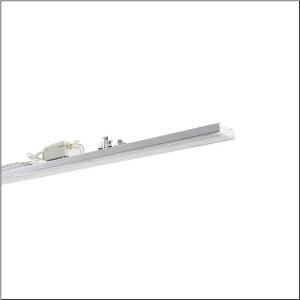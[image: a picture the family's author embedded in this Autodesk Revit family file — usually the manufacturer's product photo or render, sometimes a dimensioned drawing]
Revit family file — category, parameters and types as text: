
# Revit family: licross_r__21_recessed_mo_52te1edn495g_06d0
name_source: partatom
category: Lighting Fixtures
units: mm (PartAtom-declared; Revit-internal decimal feet)

## family parameters
Cut with Voids When Loaded = No
Host = Face
Light Source = No
Part Type = Normal
Room Calculation Point = No
Round Connector Dimension = Use Diameter
Shared = No

## types (1)
- --- (1 x LED, 9940 lm, 58 W, 4000K)
    Apparent Load = 58 VA
    CIE Flux Codes = 85 95 99 100 100
    Color Rendering = 80
    Color Temperature = 4000K
    Default Elevation = 1800 mm
    Description = Licross® 21 Recessed MO, luminaire insert, of sheet steel, galvanised, coil coated, white, length: 1.500mm, width: 66mm, height: 67mm, LED rated luminous flux: 9.940lm, light colour: 840, control gear: DALI 2, with plug, 5-pole, with phase selection, mains connection: 220..240V, AC, 50/60Hz, rated input power: 58W, halogen-free wiring, primary light control with lens, of plastic, primary optical cover: cover, of PMMA, light emission: direct distribution, primary light characteristic: symmetric, protection rating (complete): IP54, insulation class (complete): insulation class I (protective earthing), certification: CE, ENEC, VDE, UKCA, protection symbol: D if used in an environment with non-conductive dust loads with corresponding accessories, impact resistance: IK06, permissible ambient temperature for indoor applications: -25..+35°C, corresponds to IFS (International Featured Standards) requirements for safety and quality in the food industry, reducing of maximum allowable ambient temperature of 5°C with ceiling mounting, LABS conformity tested according to VDMA 24364:2018-05, packaging unit: 1 piece
    Height = 58 mm
    Lamp = 1 x LED
    Lamp Light Flux = 9940 lm
    Lamp Power = 58 W
    Lamp count = 1
    Length = 1500 mm
    Luminous efficacy = 171 lm/W
    Manufacturer = Siteco
    ModVariant = No
    Model = 52TE1EDN495G
    Mounting Place = Ceiling
    Mounting Type = Pendant
    Number of Poles = 1
    OnlyDefault = Yes
    Power Factor = 1
    Product Name = Licross® 21 Recessed MO
    Product group = luminaire insert
    ProductGroupID = 901
    Protection Class = Protection class I
    Protection Degree = IP 54
    RLX_Detail_Level = 1
    RLX_Emergency_Light_Flux = 0 lm
    RLX_Emergency_Type = 0
    RLX_Emergency_Type_DB = No
    RlxData = <blob elided: 24621 chars, md5=5b8c669a>
    Socket = socket
    Standby Power = 0 W
    System Light Flux = 9940 lm
    System Power = 58 W
    Type Comments = factory setting: luminous flux: 100 % | dim-lin: 254 | 390 mA
    Type Image = l_1296930.jpg
    URL = http://relux.com
    VarID = @adj_056547
    Voltage = 0 V
    Weight = 0.00 kg
    Width = 66 mm

## geometry (parser evidence)
native form markers: Blend x4, Sweep x9
no freeform markers — native parametric forms only
